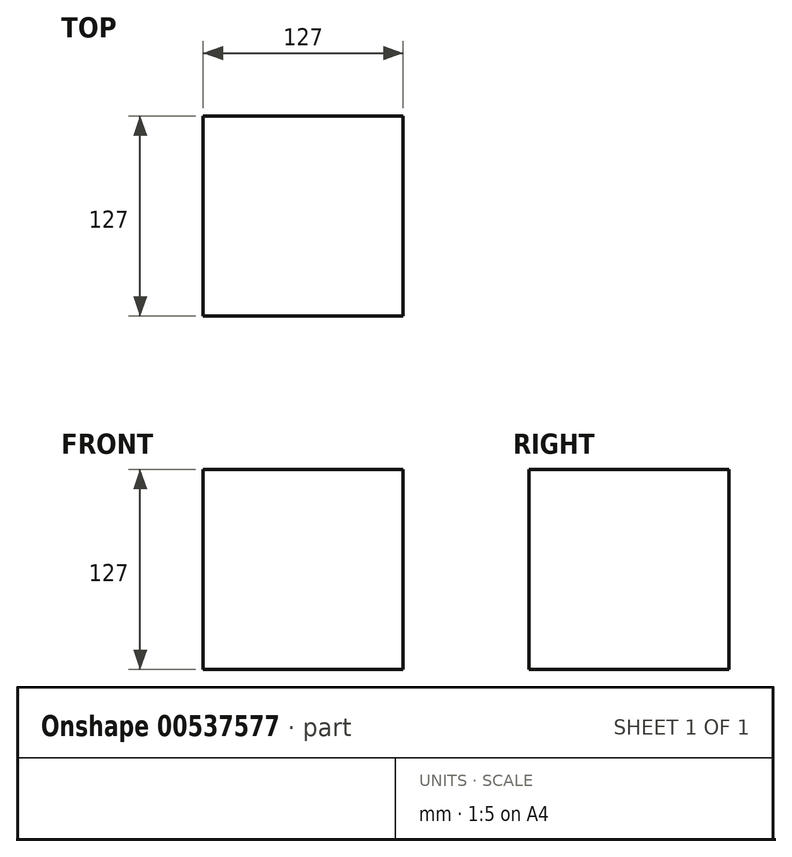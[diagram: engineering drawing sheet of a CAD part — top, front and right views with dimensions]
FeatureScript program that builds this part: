
annotation { "Feature Type Name" : "Feature", "Feature Type Description" : "" }
export const myFeature = defineFeature(function(context is Context, id is Id, definition is map)
    precondition{}
    {
        {
            var Q0;
            Q0=qCreatedBy(makeId("Top.planeOp"),FACE);
            var sketch = newSketch(context, id + "F0", { "sketchPlane" : qUnion([Q0])});
            skLineSegment(sketch, "E0.bottom", {"start": v(-63.5, 63.5) * mm, "end": v(63.5, 63.5) * mm});
            skLineSegment(sketch, "E0.top", {"start": v(-63.5, -63.5) * mm, "end": v(63.5, -63.5) * mm});
            skLineSegment(sketch, "E0.left", {"start": v(-63.5, 63.5) * mm, "end": v(-63.5, -63.5) * mm});
            skLineSegment(sketch, "E0.right", {"start": v(63.5, 63.5) * mm, "end": v(63.5, -63.5) * mm});
            skPoint(sketch, "E0.middle", {"position": v(0, 0) * mm});
            skSolve(sketch);
        }
        {
            var Q0;
            Q0 = qSketchRegion(id + "F0", true);
            extrude(context, id + "F1", {"entities" : qUnion([Q0]), "depth" : 127 * mm, "offsetDistance" : 25.4 * mm});
        }
    });
